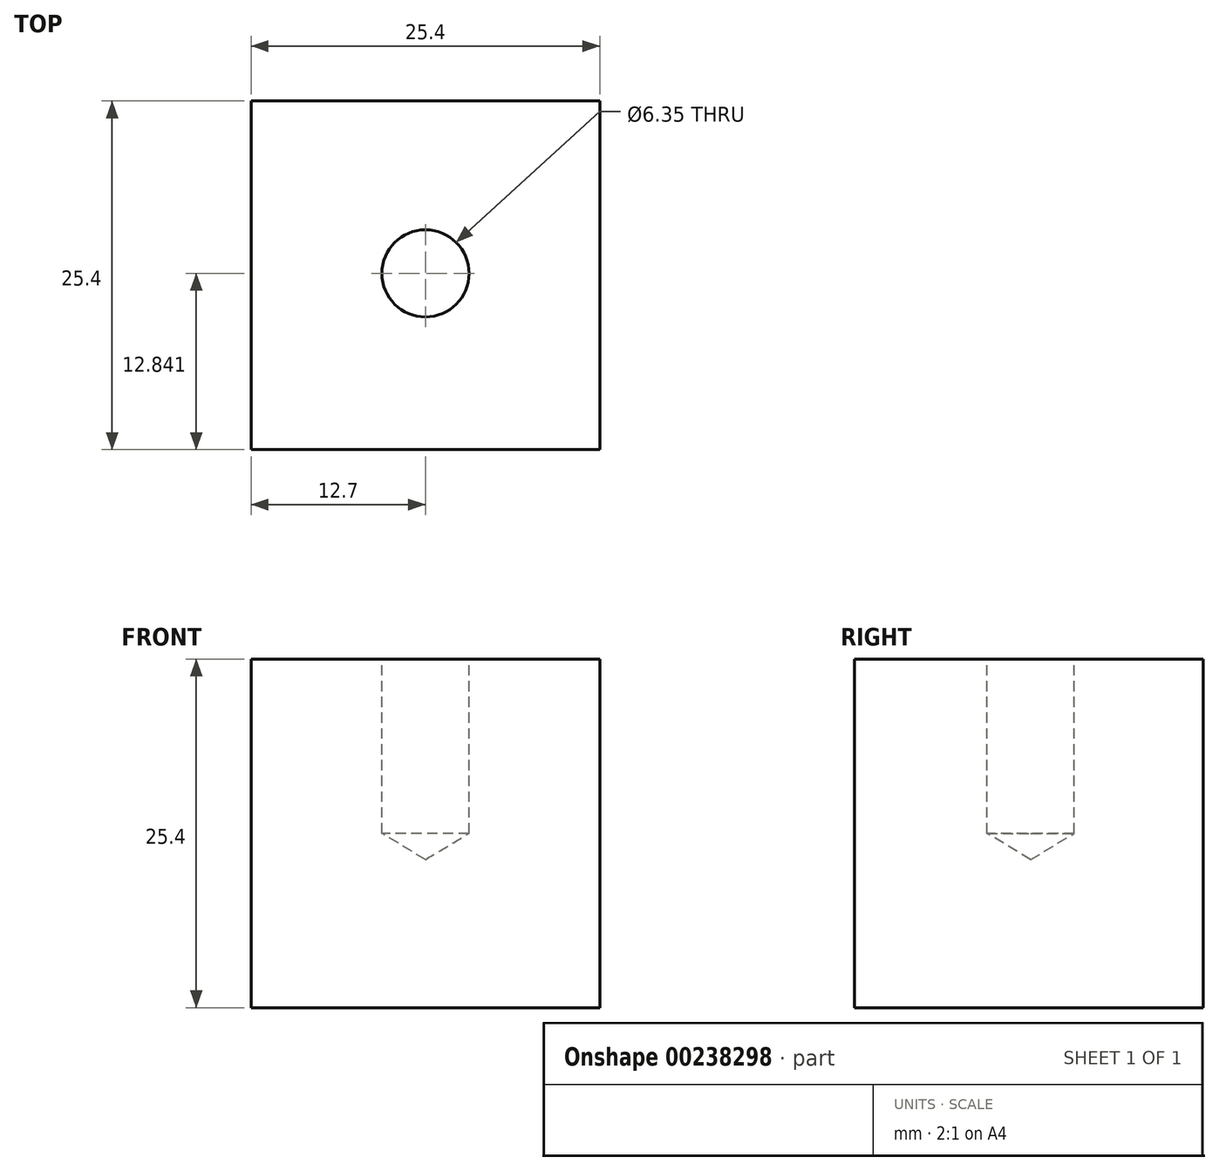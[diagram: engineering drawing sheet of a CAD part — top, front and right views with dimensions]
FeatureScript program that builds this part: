
annotation { "Feature Type Name" : "Feature", "Feature Type Description" : "" }
export const myFeature = defineFeature(function(context is Context, id is Id, definition is map)
    precondition{}
    {
        {
            var Q0;
            Q0=qCreatedBy(makeId("Top.planeOp"),FACE);
            var sketch = newSketch(context, id + "F0", { "sketchPlane" : qUnion([Q0])});
            skLineSegment(sketch, "E0.bottom", {"start": v(0, 0) * mm, "end": v(25.4, 0) * mm});
            skLineSegment(sketch, "E0.top", {"start": v(0, 25.4) * mm, "end": v(25.4, 25.4) * mm});
            skLineSegment(sketch, "E0.left", {"start": v(0, 0) * mm, "end": v(0, 25.4) * mm});
            skLineSegment(sketch, "E0.right", {"start": v(25.4, 0) * mm, "end": v(25.4, 25.4) * mm});
            skSolve(sketch);
        }
        {
            var Q0;
            Q0 = qSketchRegion(id + "F0", true);
            extrude(context, id + "F1", {"entities" : qUnion([Q0]), "depth" : 25.4 * mm});
        }
        {
            var Q0;
            Q0=makeQuery(id+"F1.opExtrude","CAP_FACE",FACE,{"disambiguationData":[OSD([sQuery(id+"F0.wireOp",EDGE,"E0.bottom"),sQuery(id+"F0.wireOp",EDGE,"E0.top"),sQuery(id+"F0.wireOp",EDGE,"E0.left"),sQuery(id+"F0.wireOp",EDGE,"E0.right")])],"isStart":false});
            var sketch = newSketch(context, id + "F2", { "sketchPlane" : qUnion([Q0])});
            skCircle(sketch, "E1", {"center": v(12.7, 12.84) * mm, "radius": 11.42 * mm});
            skPoint(sketch, "E1.centerSnap0", {"position": v(12.7, 0) * mm});
            skSolve(sketch);
        }
        {
            var Q0;
            Q0=sQuery(id+"F2.wireOp",VERTEX,"E1.center");
            var Q1;
            Q1=makeQuery(id+"F1.opExtrude","SWEPT_BODY",BODY,{"disambiguationData":[OSD([sQuery(id+"F0.wireOp",EDGE,"E0.bottom"),sQuery(id+"F0.wireOp",EDGE,"E0.top"),sQuery(id+"F0.wireOp",EDGE,"E0.left"),sQuery(id+"F0.wireOp",EDGE,"E0.right")])]});
            hole(context, id + "F3", {"style" : HoleStyle.SIMPLE, "endStyle" : HoleEndStyle.BLIND, "holeDiameter" : 6.35 * mm, "holeDepth" : 12.7 * mm, "locations" : qUnion([Q0]), "scope" : qUnion([Q1])});
        }
    });
